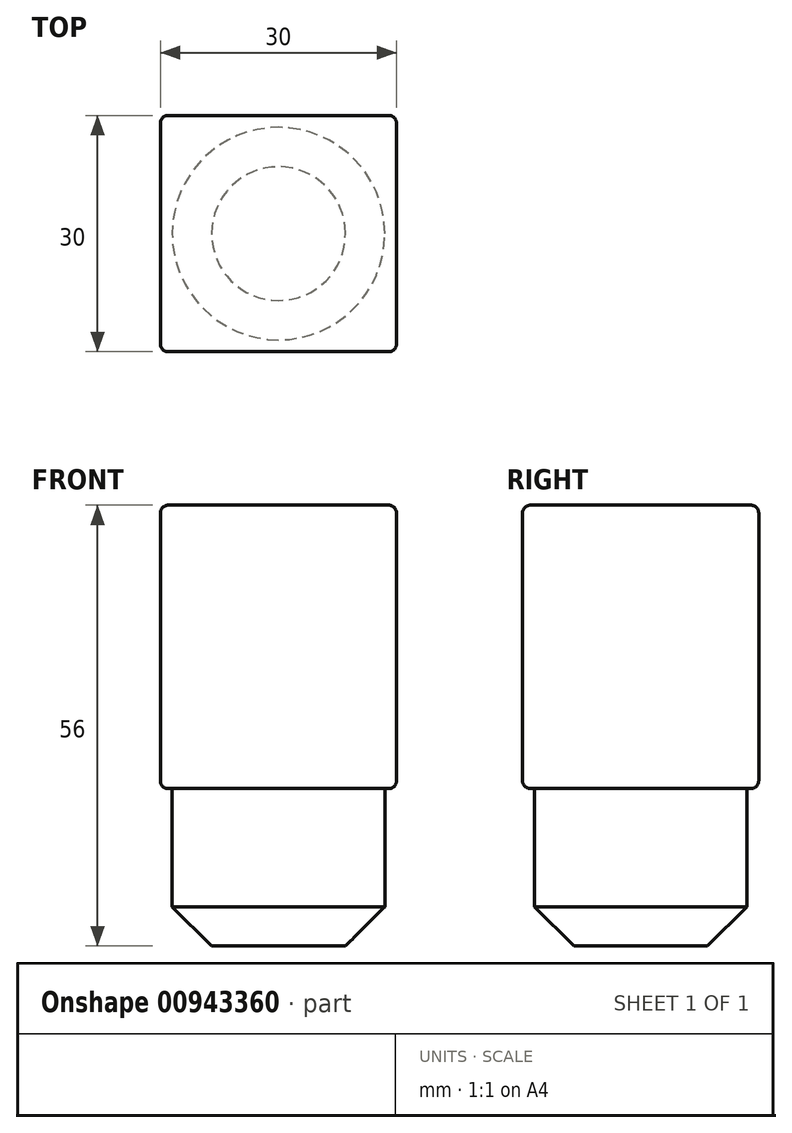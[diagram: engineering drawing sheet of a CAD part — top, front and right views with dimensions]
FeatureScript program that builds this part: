
annotation { "Feature Type Name" : "Feature", "Feature Type Description" : "" }
export const myFeature = defineFeature(function(context is Context, id is Id, definition is map)
    precondition{}
    {
        {
            var Q0;
            Q0=qCreatedBy(makeId("Top.planeOp"),FACE);
            var sketch = newSketch(context, id + "F0", { "sketchPlane" : qUnion([Q0])});
            skLineSegment(sketch, "E0.bottom", {"start": v(-15, -15) * mm, "end": v(15, -15) * mm});
            skLineSegment(sketch, "E0.top", {"start": v(-15, 15) * mm, "end": v(15, 15) * mm});
            skLineSegment(sketch, "E0.left", {"start": v(-15, -15) * mm, "end": v(-15, 15) * mm});
            skLineSegment(sketch, "E0.right", {"start": v(15, -15) * mm, "end": v(15, 15) * mm});
            skPoint(sketch, "E0.middle", {"position": v(0, 0) * mm});
            skSolve(sketch);
        }
        {
            var Q0;
            Q0=makeQuery(id+"F0.imprint","IMPRINT",FACE,{"disambiguationData":[TD([[makeQuery(id+"F0.imprint","IMPRINT",EDGE,{"derivedFrom":sQuery(id+"F0.wireOp",EDGE,"E0.bottom")}),1.0]])]});
            extrude(context, id + "F1", {"entities" : qUnion([Q0]), "depth" : 36 * mm, "offsetDistance" : 25 * mm});
        }
        {
            var Q0;
            Q0=qCreatedBy(makeId("Top.planeOp"),FACE);
            var sketch = newSketch(context, id + "F2", { "sketchPlane" : qUnion([Q0])});
            skCircle(sketch, "E1", {"center": v(0, 0) * mm, "radius": 13.5 * mm});
            skSolve(sketch);
        }
        {
            var Q0;
            Q0=makeQuery(id+"F2.imprint","IMPRINT",FACE,{"disambiguationData":[TD([[makeQuery(id+"F2.imprint","IMPRINT",EDGE,{"derivedFrom":sQuery(id+"F2.wireOp",EDGE,"E1")}),1.0]])]});
            extrude(context, id + "F3", {"entities" : qUnion([Q0]), "operationType" : NewBodyOperationType.ADD, "oppositeDirection" : true, "depth" : 20 * mm, "offsetDistance" : 25 * mm});
        }
        {
            var Q0;
            Q0=makeQuery(id+"F3.opExtrude","CAP_EDGE",EDGE,{"disambiguationData":[OSD([sQuery(id+"F2.wireOp",EDGE,"E1")])],"isStart":false});
            chamfer(context, id + "F4", {"entities" : qUnion([Q0]), "width" : 5 * mm, "tangentPropagation" : true});
        }
        {
            var Q0;
            Q0=makeQuery(id+"F1.opExtrude","CAP_EDGE",EDGE,{"disambiguationData":[OSD([sQuery(id+"F0.wireOp",EDGE,"E0.bottom")])],"isStart":true});
            var Q1;
            Q1=makeQuery(id+"F1.opExtrude","CAP_EDGE",EDGE,{"disambiguationData":[OSD([sQuery(id+"F0.wireOp",EDGE,"E0.left")])],"isStart":true});
            var Q2;
            Q2=makeQuery(id+"F1.opExtrude","CAP_EDGE",EDGE,{"disambiguationData":[OSD([sQuery(id+"F0.wireOp",EDGE,"E0.top")])],"isStart":true});
            var Q3;
            Q3=makeQuery(id+"F1.opExtrude","CAP_EDGE",EDGE,{"disambiguationData":[OSD([sQuery(id+"F0.wireOp",EDGE,"E0.right")])],"isStart":true});
            var Q4;
            Q4=makeQuery(id+"F1.opExtrude","SWEPT_EDGE",EDGE,{"disambiguationData":[OSD([sQuery(id+"F0.wireOp",EDGE,"E0.bottom"),sQuery(id+"F0.wireOp",EDGE,"E0.right")])]});
            var Q5;
            Q5=makeQuery(id+"F1.opExtrude","SWEPT_EDGE",EDGE,{"disambiguationData":[OSD([sQuery(id+"F0.wireOp",EDGE,"E0.bottom"),sQuery(id+"F0.wireOp",EDGE,"E0.left")])]});
            var Q6;
            Q6=makeQuery(id+"F1.opExtrude","SWEPT_EDGE",EDGE,{"disambiguationData":[OSD([sQuery(id+"F0.wireOp",EDGE,"E0.top"),sQuery(id+"F0.wireOp",EDGE,"E0.left")])]});
            var Q7;
            Q7=makeQuery(id+"F1.opExtrude","SWEPT_EDGE",EDGE,{"disambiguationData":[OSD([sQuery(id+"F0.wireOp",EDGE,"E0.top"),sQuery(id+"F0.wireOp",EDGE,"E0.right")])]});
            var Q8;
            Q8=makeQuery(id+"F1.opExtrude","CAP_EDGE",EDGE,{"disambiguationData":[OSD([sQuery(id+"F0.wireOp",EDGE,"E0.bottom")])],"isStart":false});
            var Q9;
            Q9=makeQuery(id+"F1.opExtrude","CAP_EDGE",EDGE,{"disambiguationData":[OSD([sQuery(id+"F0.wireOp",EDGE,"E0.left")])],"isStart":false});
            var Q10;
            Q10=makeQuery(id+"F1.opExtrude","CAP_EDGE",EDGE,{"disambiguationData":[OSD([sQuery(id+"F0.wireOp",EDGE,"E0.right")])],"isStart":false});
            var Q11;
            Q11=makeQuery(id+"F1.opExtrude","CAP_EDGE",EDGE,{"disambiguationData":[OSD([sQuery(id+"F0.wireOp",EDGE,"E0.top")])],"isStart":false});
            fillet(context, id + "F5", {"entities" : qUnion([Q0, Q1, Q2, Q3, Q4, Q5, Q6, Q7, Q8, Q9, Q10, Q11]), "radius" : 1 * mm, "tangentPropagation" : true, "allowEdgeOverflow" : false});
        }
    });
